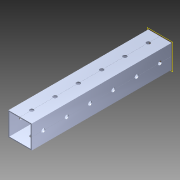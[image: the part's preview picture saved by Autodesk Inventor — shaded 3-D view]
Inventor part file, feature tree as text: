
AUTODESK INVENTOR PART (.ipt)
format: ipt  version: 2014 (Build 180170000, 170)  size: 1,138,688 bytes
history: native  units: in
note: dims shown in document units (in); Inventor stores cm internally (conversion verified against a paired STEP export)
features: pattern_circular x1, other x1, plane x1, extrude x1, imported_body x1, sketch x1
ambient origin geometry x8: Origin, YZ Plane, XZ Plane, XY Plane, X Axis, Y Axis, Z Axis, Center Point
bodies: Body1 (feature_tree)
feature tree (6):
  pattern_circular  "CirPattern2"
  other  "217-3426-STEP1"
  plane  "Work Plane1"
  extrude  "Extrusion1"  Depth=3937.0079in TaperAngle=0.0deg
  imported_body  "Base1"
  sketch  "Sketch1"  dims[d0=-6.0in d1=3937.0079in d2=0.0in]
